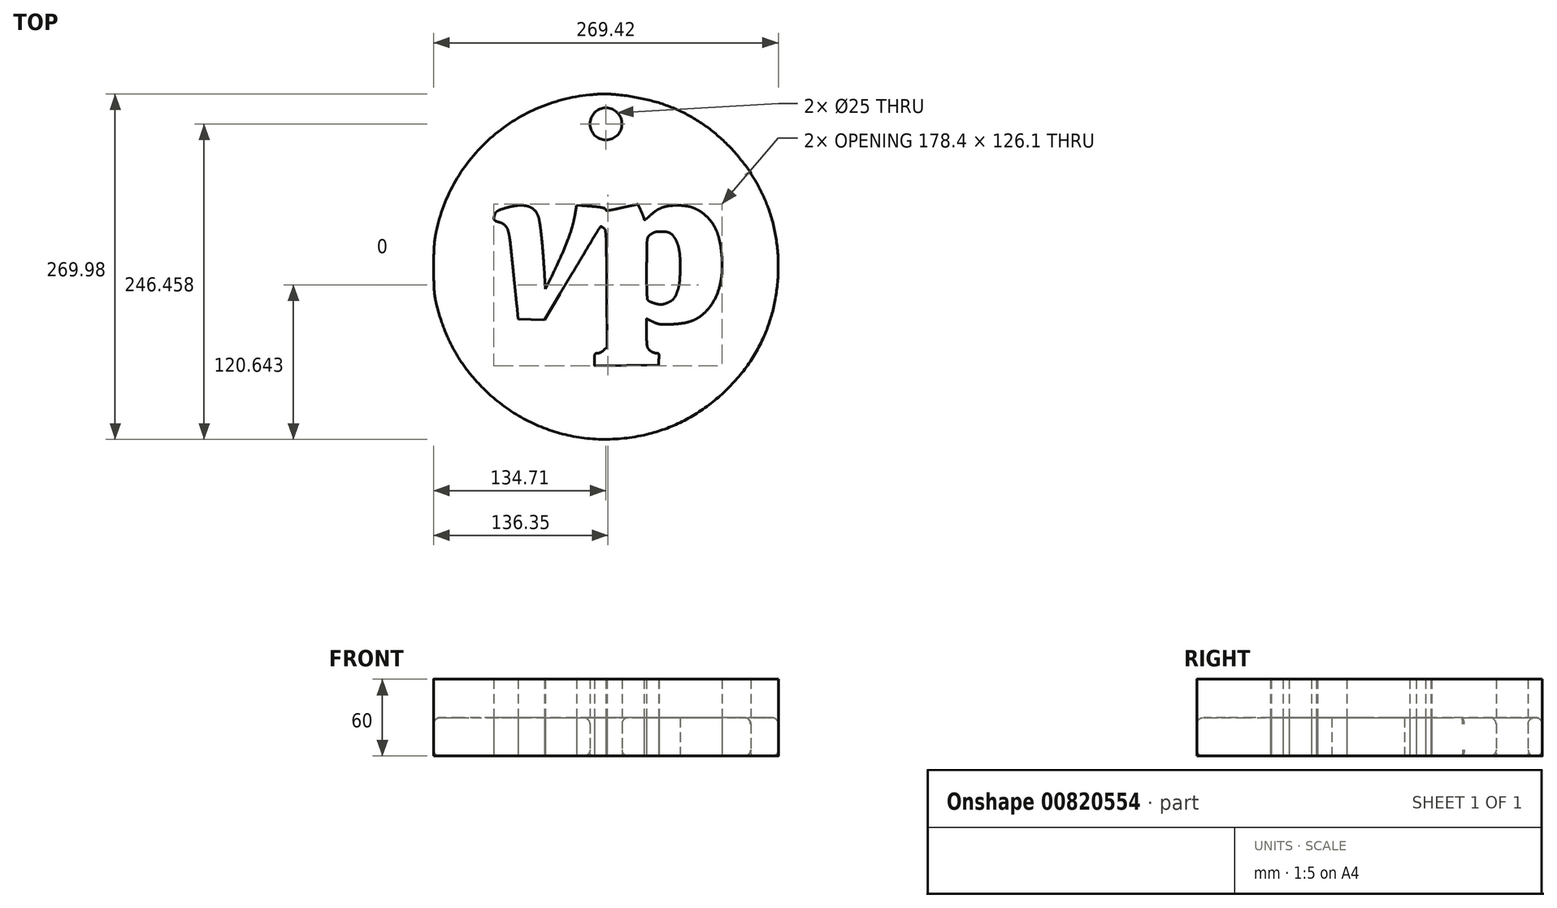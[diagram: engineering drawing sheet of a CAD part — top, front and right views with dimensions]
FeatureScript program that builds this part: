
annotation { "Feature Type Name" : "Feature", "Feature Type Description" : "" }
export const myFeature = defineFeature(function(context is Context, id is Id, definition is map)
    precondition{}
    {
        {
            var Q0;
            Q0=qCreatedBy(makeId("Top.planeOp"),FACE);
            var sketch = newSketch(context, id + "F0", { "sketchPlane" : qUnion([Q0])});
            skArc(sketch, "E0", {"start": v(-12.8, 134.12) * mm, "mid": v(-33.97, 130.4) * mm, "end": v(-54.29, 123.36) * mm});
            skArc(sketch, "E1", {"start": v(-54.29, 123.36) * mm, "mid": v(-73.28, 113.18) * mm, "end": v(-90.43, 100.15) * mm});
            skArc(sketch, "E2", {"start": v(-90.43, 100.15) * mm, "mid": v(-105.3, 84.59) * mm, "end": v(-117.52, 66.88) * mm});
            skArc(sketch, "E3", {"start": v(-117.52, 66.88) * mm, "mid": v(-126.75, 47.53) * mm, "end": v(-132.77, 26.96) * mm});
            skArc(sketch, "E4", {"start": v(-132.77, 26.96) * mm, "mid": v(-133.74, 21.22) * mm, "end": v(-134.27, 15.41) * mm});
            skArc(sketch, "E5", {"start": v(-134.27, 15.41) * mm, "mid": v(-134.6, 7.1) * mm, "end": v(-134.7, -1.22) * mm});
            skArc(sketch, "E6", {"start": v(-134.7, -1.22) * mm, "mid": v(-134.6, -9.46) * mm, "end": v(-134.26, -17.69) * mm});
            skArc(sketch, "E7", {"start": v(-134.26, -17.69) * mm, "mid": v(-133.73, -23.05) * mm, "end": v(-132.73, -28.35) * mm});
            skArc(sketch, "E8", {"start": v(-132.73, -28.35) * mm, "mid": v(-130.15, -37.94) * mm, "end": v(-126.97, -47.34) * mm});
            skArc(sketch, "E9", {"start": v(-126.97, -47.34) * mm, "mid": v(-123.33, -56.1) * mm, "end": v(-119.06, -64.58) * mm});
            skArc(sketch, "E10", {"start": v(-119.06, -64.58) * mm, "mid": v(-114.25, -72.64) * mm, "end": v(-108.86, -80.33) * mm});
            skArc(sketch, "E11", {"start": v(-108.86, -80.33) * mm, "mid": v(-102.8, -87.8) * mm, "end": v(-96.25, -94.83) * mm});
            skArc(sketch, "E12", {"start": v(-96.25, -94.83) * mm, "mid": v(-82.95, -106.58) * mm, "end": v(-68.27, -116.56) * mm});
            skArc(sketch, "E13", {"start": v(-68.27, -116.56) * mm, "mid": v(-52.65, -124.44) * mm, "end": v(-36.12, -130.2) * mm});
            skArc(sketch, "E14", {"start": v(-36.12, -130.2) * mm, "mid": v(-18.96, -133.74) * mm, "end": v(-1.48, -134.98) * mm});
            skArc(sketch, "E15", {"start": v(-1.48, -134.98) * mm, "mid": v(16.29, -133.96) * mm, "end": v(33.8, -130.7) * mm});
            skArc(sketch, "E16", {"start": v(33.8, -130.7) * mm, "mid": v(47.8, -126.28) * mm, "end": v(61.2, -120.25) * mm});
            skArc(sketch, "E17", {"start": v(61.2, -120.25) * mm, "mid": v(74.24, -112.5) * mm, "end": v(86.38, -103.4) * mm});
            skArc(sketch, "E18", {"start": v(86.38, -103.4) * mm, "mid": v(97.5, -93.04) * mm, "end": v(107.44, -81.55) * mm});
            skArc(sketch, "E19", {"start": v(107.44, -81.55) * mm, "mid": v(115.81, -69.37) * mm, "end": v(122.71, -56.3) * mm});
            skArc(sketch, "E20", {"start": v(122.71, -56.3) * mm, "mid": v(127.5, -44.26) * mm, "end": v(131.05, -31.81) * mm});
            skArc(sketch, "E21", {"start": v(131.05, -31.81) * mm, "mid": v(133.43, -18.82) * mm, "end": v(134.6, -5.67) * mm});
            skArc(sketch, "E22", {"start": v(134.6, -5.67) * mm, "mid": v(134.51, 7.53) * mm, "end": v(133.2, 20.65) * mm});
            skArc(sketch, "E23", {"start": v(133.2, 20.65) * mm, "mid": v(130.67, 33.3) * mm, "end": v(126.9, 45.64) * mm});
            skArc(sketch, "E24", {"start": v(126.9, 45.64) * mm, "mid": v(125.79, 48.55) * mm, "end": v(124.59, 51.42) * mm});
            skArc(sketch, "E25", {"start": v(124.59, 51.42) * mm, "mid": v(123.09, 54.78) * mm, "end": v(121.52, 58.1) * mm});
            skArc(sketch, "E26", {"start": v(121.52, 58.1) * mm, "mid": v(119.97, 61.25) * mm, "end": v(118.36, 64.35) * mm});
            skArc(sketch, "E27", {"start": v(118.36, 64.35) * mm, "mid": v(117.17, 66.46) * mm, "end": v(115.86, 68.5) * mm});
            skArc(sketch, "E28", {"start": v(115.86, 68.5) * mm, "mid": v(115.38, 69.22) * mm, "end": v(114.9, 69.95) * mm});
            skArc(sketch, "E29", {"start": v(114.9, 69.95) * mm, "mid": v(114.5, 70.6) * mm, "end": v(114.1, 71.25) * mm});
            skArc(sketch, "E30", {"start": v(114.1, 71.25) * mm, "mid": v(113.78, 71.8) * mm, "end": v(113.46, 72.36) * mm});
            skArc(sketch, "E31", {"start": v(113.46, 72.36) * mm, "mid": v(113.4, 72.52) * mm, "end": v(113.37, 72.7) * mm});
            skArc(sketch, "E32", {"start": v(113.37, 72.7) * mm, "mid": v(113.25, 73.44) * mm, "end": v(112.89, 74.1) * mm});
            skArc(sketch, "E33", {"start": v(112.89, 74.1) * mm, "mid": v(110.07, 77.7) * mm, "end": v(107.23, 81.3) * mm});
            skArc(sketch, "E34", {"start": v(107.23, 81.3) * mm, "mid": v(104.44, 84.76) * mm, "end": v(101.6, 88.17) * mm});
            skArc(sketch, "E35", {"start": v(101.6, 88.17) * mm, "mid": v(99.42, 90.68) * mm, "end": v(97.16, 93.11) * mm});
            skArc(sketch, "E36", {"start": v(97.16, 93.11) * mm, "mid": v(88.23, 101.61) * mm, "end": v(78.6, 109.3) * mm});
            skArc(sketch, "E37", {"start": v(78.6, 109.3) * mm, "mid": v(68.62, 115.87) * mm, "end": v(58.07, 121.46) * mm});
            skArc(sketch, "E38", {"start": v(58.07, 121.46) * mm, "mid": v(46.83, 126.1) * mm, "end": v(35.2, 129.69) * mm});
            skArc(sketch, "E39", {"start": v(35.2, 129.69) * mm, "mid": v(22.52, 132.43) * mm, "end": v(9.67, 134.2) * mm});
            skArc(sketch, "E40", {"start": v(9.67, 134.2) * mm, "mid": v(6.1, 134.53) * mm, "end": v(2.54, 134.84) * mm});
            skArc(sketch, "E41", {"start": v(2.54, 134.84) * mm, "mid": v(0.68, 134.95) * mm, "end": v(-1.18, 134.99) * mm});
            skArc(sketch, "E42", {"start": v(-1.18, 134.99) * mm, "mid": v(-3.09, 134.94) * mm, "end": v(-5, 134.82) * mm});
            skArc(sketch, "E43", {"start": v(-5, 134.82) * mm, "mid": v(-8.9, 134.48) * mm, "end": v(-12.8, 134.12) * mm});
            skArc(sketch, "E44", {"start": v(27.46, 43.43) * mm, "mid": v(27.93, 42.36) * mm, "end": v(28.4, 41.28) * mm});
            skArc(sketch, "E45", {"start": v(28.4, 41.28) * mm, "mid": v(28.8, 40.26) * mm, "end": v(29.19, 39.24) * mm});
            skArc(sketch, "E46", {"start": v(29.19, 39.24) * mm, "mid": v(29.5, 38.38) * mm, "end": v(29.78, 37.52) * mm});
            skArc(sketch, "E47", {"start": v(29.78, 37.52) * mm, "mid": v(29.88, 37.11) * mm, "end": v(29.9, 36.7) * mm});
            skArc(sketch, "E48", {"start": v(29.9, 36.7) * mm, "mid": v(30.02, 36.5) * mm, "end": v(30.24, 36.5) * mm});
            skArc(sketch, "E49", {"start": v(30.24, 36.5) * mm, "mid": v(30.8, 36.78) * mm, "end": v(31.32, 37.12) * mm});
            skArc(sketch, "E50", {"start": v(31.32, 37.12) * mm, "mid": v(32.11, 37.7) * mm, "end": v(32.87, 38.32) * mm});
            skArc(sketch, "E51", {"start": v(32.87, 38.32) * mm, "mid": v(33.8, 39.16) * mm, "end": v(34.72, 40.02) * mm});
            skArc(sketch, "E52", {"start": v(34.72, 40.02) * mm, "mid": v(36.88, 41.95) * mm, "end": v(39.2, 43.67) * mm});
            skArc(sketch, "E53", {"start": v(39.2, 43.67) * mm, "mid": v(41.45, 45) * mm, "end": v(43.85, 46.07) * mm});
            skArc(sketch, "E54", {"start": v(43.85, 46.07) * mm, "mid": v(46.47, 46.88) * mm, "end": v(49.17, 47.4) * mm});
            skArc(sketch, "E55", {"start": v(49.17, 47.4) * mm, "mid": v(52.42, 47.72) * mm, "end": v(55.69, 47.83) * mm});
            skArc(sketch, "E56", {"start": v(55.69, 47.83) * mm, "mid": v(59.02, 47.72) * mm, "end": v(62.34, 47.38) * mm});
            skArc(sketch, "E57", {"start": v(62.34, 47.38) * mm, "mid": v(65.17, 46.85) * mm, "end": v(67.93, 46.03) * mm});
            skArc(sketch, "E58", {"start": v(67.93, 46.03) * mm, "mid": v(70.5, 44.95) * mm, "end": v(72.93, 43.6) * mm});
            skArc(sketch, "E59", {"start": v(72.93, 43.6) * mm, "mid": v(75.43, 41.9) * mm, "end": v(77.77, 39.97) * mm});
            skArc(sketch, "E60", {"start": v(77.77, 39.97) * mm, "mid": v(80.12, 37.67) * mm, "end": v(82.25, 35.16) * mm});
            skArc(sketch, "E61", {"start": v(82.25, 35.16) * mm, "mid": v(84.07, 32.52) * mm, "end": v(85.6, 29.71) * mm});
            skArc(sketch, "E62", {"start": v(85.6, 29.71) * mm, "mid": v(86.97, 26.54) * mm, "end": v(88.03, 23.24) * mm});
            skArc(sketch, "E63", {"start": v(88.03, 23.24) * mm, "mid": v(88.99, 19.3) * mm, "end": v(89.7, 15.32) * mm});
            skArc(sketch, "E64", {"start": v(89.7, 15.32) * mm, "mid": v(90.58, 7.55) * mm, "end": v(90.84, -0.27) * mm});
            skArc(sketch, "E65", {"start": v(90.84, -0.27) * mm, "mid": v(90.4, -7.21) * mm, "end": v(89.21, -14.07) * mm});
            skArc(sketch, "E66", {"start": v(89.21, -14.07) * mm, "mid": v(87.42, -20.08) * mm, "end": v(84.88, -25.8) * mm});
            skArc(sketch, "E67", {"start": v(84.88, -25.8) * mm, "mid": v(81.8, -30.79) * mm, "end": v(77.98, -35.24) * mm});
            skArc(sketch, "E68", {"start": v(77.98, -35.24) * mm, "mid": v(75.47, -37.52) * mm, "end": v(72.75, -39.55) * mm});
            skArc(sketch, "E69", {"start": v(72.75, -39.55) * mm, "mid": v(70.03, -41.17) * mm, "end": v(67.14, -42.45) * mm});
            skArc(sketch, "E70", {"start": v(67.14, -42.45) * mm, "mid": v(63.81, -43.5) * mm, "end": v(60.4, -44.21) * mm});
            skArc(sketch, "E71", {"start": v(60.4, -44.21) * mm, "mid": v(56.05, -44.77) * mm, "end": v(51.67, -45.1) * mm});
            skArc(sketch, "E72", {"start": v(51.67, -45.1) * mm, "mid": v(48.8, -45.22) * mm, "end": v(45.94, -45.3) * mm});
            skArc(sketch, "E73", {"start": v(45.94, -45.3) * mm, "mid": v(44.32, -45.27) * mm, "end": v(42.7, -45.13) * mm});
            skArc(sketch, "E74", {"start": v(42.7, -45.13) * mm, "mid": v(41.4, -44.9) * mm, "end": v(40.13, -44.54) * mm});
            skArc(sketch, "E75", {"start": v(40.13, -44.54) * mm, "mid": v(38.6, -43.98) * mm, "end": v(37.11, -43.32) * mm});
            skArc(sketch, "E76", {"start": v(37.11, -43.32) * mm, "mid": v(36.18, -42.88) * mm, "end": v(35.25, -42.44) * mm});
            skArc(sketch, "E77", {"start": v(35.25, -42.44) * mm, "mid": v(34.42, -42.04) * mm, "end": v(33.6, -41.65) * mm});
            skArc(sketch, "E78", {"start": v(33.6, -41.65) * mm, "mid": v(32.9, -41.3) * mm, "end": v(32.2, -40.97) * mm});
            skArc(sketch, "E79", {"start": v(32.2, -40.97) * mm, "mid": v(32.02, -40.88) * mm, "end": v(31.85, -40.78) * mm});
            skArc(sketch, "E80", {"start": v(31.85, -40.78) * mm, "mid": v(31.73, -40.77) * mm, "end": v(31.66, -40.88) * mm});
            skArc(sketch, "E81", {"start": v(31.66, -40.88) * mm, "mid": v(31.62, -42.43) * mm, "end": v(31.6, -43.98) * mm});
            skArc(sketch, "E82", {"start": v(31.6, -43.98) * mm, "mid": v(31.58, -45.82) * mm, "end": v(31.58, -47.67) * mm});
            skArc(sketch, "E83", {"start": v(31.58, -47.67) * mm, "mid": v(31.62, -49.89) * mm, "end": v(31.66, -52.1) * mm});
            skArc(sketch, "E84", {"start": v(31.66, -52.1) * mm, "mid": v(31.77, -55.76) * mm, "end": v(31.9, -59.42) * mm});
            skArc(sketch, "E85", {"start": v(31.9, -59.42) * mm, "mid": v(32.03, -60.9) * mm, "end": v(32.27, -62.38) * mm});
            skArc(sketch, "E86", {"start": v(32.27, -62.38) * mm, "mid": v(32.56, -63.3) * mm, "end": v(33.02, -64.15) * mm});
            skArc(sketch, "E87", {"start": v(33.02, -64.15) * mm, "mid": v(33.69, -64.98) * mm, "end": v(34.46, -65.7) * mm});
            skArc(sketch, "E88", {"start": v(34.46, -65.7) * mm, "mid": v(35.01, -66.1) * mm, "end": v(35.6, -66.45) * mm});
            skArc(sketch, "E89", {"start": v(35.6, -66.45) * mm, "mid": v(36.25, -66.78) * mm, "end": v(36.92, -67.08) * mm});
            skArc(sketch, "E90", {"start": v(36.92, -67.08) * mm, "mid": v(37.57, -67.32) * mm, "end": v(38.23, -67.52) * mm});
            skArc(sketch, "E91", {"start": v(38.23, -67.52) * mm, "mid": v(38.77, -67.62) * mm, "end": v(39.31, -67.66) * mm});
            skArc(sketch, "E92", {"start": v(39.31, -67.66) * mm, "mid": v(39.98, -67.7) * mm, "end": v(40.64, -67.82) * mm});
            skArc(sketch, "E93", {"start": v(40.64, -67.82) * mm, "mid": v(41.02, -68.01) * mm, "end": v(41.27, -68.35) * mm});
            skArc(sketch, "E94", {"start": v(41.27, -68.35) * mm, "mid": v(41.44, -68.89) * mm, "end": v(41.49, -69.45) * mm});
            skArc(sketch, "E95", {"start": v(41.49, -69.45) * mm, "mid": v(41.44, -70.86) * mm, "end": v(41.37, -72.27) * mm});
            skLineSegment(sketch, "E96", {"start": v(41.37, -72.27) * mm, "end": v(41.07, -76.88) * mm});
            skLineSegment(sketch, "E97", {"start": v(41.07, -76.88) * mm, "end": v(16.08, -77.14) * mm});
            skLineSegment(sketch, "E98", {"start": v(16.08, -77.14) * mm, "end": v(-8.9, -77.4) * mm});
            skLineSegment(sketch, "E99", {"start": v(-8.9, -77.4) * mm, "end": v(-8.9, -72.53) * mm});
            skArc(sketch, "E100", {"start": v(-8.9, -72.53) * mm, "mid": v(-8.9, -71.04) * mm, "end": v(-8.85, -69.55) * mm});
            skArc(sketch, "E101", {"start": v(-8.85, -69.55) * mm, "mid": v(-8.76, -68.95) * mm, "end": v(-8.54, -68.38) * mm});
            skArc(sketch, "E102", {"start": v(-8.54, -68.38) * mm, "mid": v(-8.26, -68.03) * mm, "end": v(-7.85, -67.83) * mm});
            skArc(sketch, "E103", {"start": v(-7.85, -67.83) * mm, "mid": v(-7.15, -67.7) * mm, "end": v(-6.44, -67.66) * mm});
            skArc(sketch, "E104", {"start": v(-6.44, -67.66) * mm, "mid": v(-5.87, -67.62) * mm, "end": v(-5.32, -67.49) * mm});
            skArc(sketch, "E105", {"start": v(-5.32, -67.49) * mm, "mid": v(-4.64, -67.24) * mm, "end": v(-3.99, -66.95) * mm});
            skArc(sketch, "E106", {"start": v(-3.99, -66.95) * mm, "mid": v(-3.31, -66.59) * mm, "end": v(-2.66, -66.17) * mm});
            skArc(sketch, "E107", {"start": v(-2.66, -66.17) * mm, "mid": v(-2.1, -65.74) * mm, "end": v(-1.56, -65.25) * mm});
            skLineSegment(sketch, "E108", {"start": v(-1.56, -65.25) * mm, "end": v(0.85, -62.84) * mm});
            skLineSegment(sketch, "E109", {"start": v(0.85, -62.84) * mm, "end": v(0.58, -17.13) * mm});
            skArc(sketch, "E110", {"start": v(0.58, -17.13) * mm, "mid": v(0.48, -2.6) * mm, "end": v(0.37, 11.92) * mm});
            skArc(sketch, "E111", {"start": v(0.37, 11.92) * mm, "mid": v(0.28, 17.16) * mm, "end": v(0.08, 22.4) * mm});
            skArc(sketch, "E112", {"start": v(0.08, 22.4) * mm, "mid": v(-0.1, 25.2) * mm, "end": v(-0.4, 27.97) * mm});
            skArc(sketch, "E113", {"start": v(-0.4, 27.97) * mm, "mid": v(-0.78, 29.08) * mm, "end": v(-1.57, 29.95) * mm});
            skArc(sketch, "E114", {"start": v(-1.57, 29.95) * mm, "mid": v(-1.95, 30.22) * mm, "end": v(-2.34, 30.48) * mm});
            skArc(sketch, "E115", {"start": v(-2.34, 30.48) * mm, "mid": v(-2.7, 30.7) * mm, "end": v(-3.07, 30.93) * mm});
            skArc(sketch, "E116", {"start": v(-3.07, 30.93) * mm, "mid": v(-3.38, 31.1) * mm, "end": v(-3.7, 31.26) * mm});
            skArc(sketch, "E117", {"start": v(-3.7, 31.26) * mm, "mid": v(-3.85, 31.31) * mm, "end": v(-4.02, 31.33) * mm});
            skArc(sketch, "E118", {"start": v(-4.02, 31.33) * mm, "mid": v(-4.2, 31.28) * mm, "end": v(-4.35, 31.15) * mm});
            skArc(sketch, "E119", {"start": v(-4.35, 31.15) * mm, "mid": v(-5.45, 29.44) * mm, "end": v(-6.55, 27.73) * mm});
            skArc(sketch, "E120", {"start": v(-6.55, 27.73) * mm, "mid": v(-7.79, 25.76) * mm, "end": v(-9.01, 23.77) * mm});
            skArc(sketch, "E121", {"start": v(-9.01, 23.77) * mm, "mid": v(-10.43, 21.43) * mm, "end": v(-11.84, 19.07) * mm});
            skArc(sketch, "E122", {"start": v(-11.84, 19.07) * mm, "mid": v(-14.73, 14.19) * mm, "end": v(-17.63, 9.3) * mm});
            skArc(sketch, "E123", {"start": v(-17.63, 9.3) * mm, "mid": v(-19.57, 6.04) * mm, "end": v(-21.52, 2.78) * mm});
            skArc(sketch, "E124", {"start": v(-21.52, 2.78) * mm, "mid": v(-23.82, -1.06) * mm, "end": v(-26.12, -4.9) * mm});
            skArc(sketch, "E125", {"start": v(-26.12, -4.9) * mm, "mid": v(-31.08, -13.15) * mm, "end": v(-36.04, -21.4) * mm});
            skLineSegment(sketch, "E126", {"start": v(-36.04, -21.4) * mm, "end": v(-48.14, -41.52) * mm});
            skLineSegment(sketch, "E127", {"start": v(-48.14, -41.52) * mm, "end": v(-58.37, -41.24) * mm});
            skLineSegment(sketch, "E128", {"start": v(-58.37, -41.24) * mm, "end": v(-68.6, -40.97) * mm});
            skLineSegment(sketch, "E129", {"start": v(-68.6, -40.97) * mm, "end": v(-69.72, -30.3) * mm});
            skArc(sketch, "E130", {"start": v(-69.72, -30.3) * mm, "mid": v(-69.99, -27.7) * mm, "end": v(-70.25, -25.12) * mm});
            skArc(sketch, "E131", {"start": v(-70.25, -25.12) * mm, "mid": v(-70.6, -21.66) * mm, "end": v(-70.96, -18.21) * mm});
            skArc(sketch, "E132", {"start": v(-70.96, -18.21) * mm, "mid": v(-71.34, -14.53) * mm, "end": v(-71.71, -10.85) * mm});
            skArc(sketch, "E133", {"start": v(-71.71, -10.85) * mm, "mid": v(-72.05, -7.5) * mm, "end": v(-72.39, -4.14) * mm});
            skArc(sketch, "E134", {"start": v(-72.39, -4.14) * mm, "mid": v(-73.64, 8.02) * mm, "end": v(-74.96, 20.19) * mm});
            skArc(sketch, "E135", {"start": v(-74.96, 20.19) * mm, "mid": v(-75.6, 24.34) * mm, "end": v(-76.58, 28.42) * mm});
            skArc(sketch, "E136", {"start": v(-76.58, 28.42) * mm, "mid": v(-77.55, 30.6) * mm, "end": v(-79.1, 32.42) * mm});
            skArc(sketch, "E137", {"start": v(-79.1, 32.42) * mm, "mid": v(-81.14, 33.82) * mm, "end": v(-83.48, 34.67) * mm});
            skArc(sketch, "E138", {"start": v(-83.48, 34.67) * mm, "mid": v(-84.8, 35.04) * mm, "end": v(-86.1, 35.52) * mm});
            skArc(sketch, "E139", {"start": v(-86.1, 35.52) * mm, "mid": v(-86.8, 35.99) * mm, "end": v(-87.3, 36.67) * mm});
            skArc(sketch, "E140", {"start": v(-87.3, 36.67) * mm, "mid": v(-87.54, 37.52) * mm, "end": v(-87.5, 38.4) * mm});
            skArc(sketch, "E141", {"start": v(-87.5, 38.4) * mm, "mid": v(-87.12, 39.86) * mm, "end": v(-86.64, 41.3) * mm});
            skArc(sketch, "E142", {"start": v(-86.64, 41.3) * mm, "mid": v(-86.3, 41.96) * mm, "end": v(-85.83, 42.54) * mm});
            skArc(sketch, "E143", {"start": v(-85.83, 42.54) * mm, "mid": v(-85.19, 43.1) * mm, "end": v(-84.47, 43.57) * mm});
            skArc(sketch, "E144", {"start": v(-84.47, 43.57) * mm, "mid": v(-83.4, 44.1) * mm, "end": v(-82.27, 44.55) * mm});
            skArc(sketch, "E145", {"start": v(-82.27, 44.55) * mm, "mid": v(-80.46, 45.16) * mm, "end": v(-78.63, 45.72) * mm});
            skArc(sketch, "E146", {"start": v(-78.63, 45.72) * mm, "mid": v(-74.03, 46.89) * mm, "end": v(-69.34, 47.68) * mm});
            skArc(sketch, "E147", {"start": v(-69.34, 47.68) * mm, "mid": v(-65.65, 47.83) * mm, "end": v(-61.99, 47.36) * mm});
            skArc(sketch, "E148", {"start": v(-61.99, 47.36) * mm, "mid": v(-59.17, 46.41) * mm, "end": v(-56.65, 44.84) * mm});
            skArc(sketch, "E149", {"start": v(-56.65, 44.84) * mm, "mid": v(-54.67, 42.78) * mm, "end": v(-53.28, 40.29) * mm});
            skArc(sketch, "E150", {"start": v(-53.28, 40.29) * mm, "mid": v(-52.5, 37.98) * mm, "end": v(-52, 35.6) * mm});
            skArc(sketch, "E151", {"start": v(-52, 35.6) * mm, "mid": v(-51.32, 31.17) * mm, "end": v(-50.74, 26.71) * mm});
            skArc(sketch, "E152", {"start": v(-50.74, 26.71) * mm, "mid": v(-50.08, 20.76) * mm, "end": v(-49.53, 14.8) * mm});
            skArc(sketch, "E153", {"start": v(-49.53, 14.8) * mm, "mid": v(-48.92, 7.05) * mm, "end": v(-48.37, -0.7) * mm});
            skLineSegment(sketch, "E154", {"start": v(-48.37, -0.7) * mm, "end": v(-47.23, -17.68) * mm});
            skLineSegment(sketch, "E155", {"start": v(-47.23, -17.68) * mm, "end": v(-43.5, -9.92) * mm});
            skArc(sketch, "E156", {"start": v(-43.5, -9.92) * mm, "mid": v(-39.32, -1.12) * mm, "end": v(-35.25, 7.73) * mm});
            skArc(sketch, "E157", {"start": v(-35.25, 7.73) * mm, "mid": v(-32.43, 14.2) * mm, "end": v(-29.82, 20.76) * mm});
            skArc(sketch, "E158", {"start": v(-29.82, 20.76) * mm, "mid": v(-27.96, 25.96) * mm, "end": v(-26.31, 31.24) * mm});
            skArc(sketch, "E159", {"start": v(-26.31, 31.24) * mm, "mid": v(-25.13, 35.87) * mm, "end": v(-24.25, 40.57) * mm});
            skLineSegment(sketch, "E160", {"start": v(-24.25, 40.57) * mm, "end": v(-23.09, 48.03) * mm});
            skLineSegment(sketch, "E161", {"start": v(-23.09, 48.03) * mm, "end": v(-14.79, 47.39) * mm});
            skArc(sketch, "E162", {"start": v(-14.79, 47.39) * mm, "mid": v(-11.04, 47.08) * mm, "end": v(-7.3, 46.73) * mm});
            skArc(sketch, "E163", {"start": v(-7.3, 46.73) * mm, "mid": v(-5.22, 46.48) * mm, "end": v(-3.16, 46.12) * mm});
            skArc(sketch, "E164", {"start": v(-3.16, 46.12) * mm, "mid": v(-1.98, 45.82) * mm, "end": v(-0.83, 45.4) * mm});
            skArc(sketch, "E165", {"start": v(-0.83, 45.4) * mm, "mid": v(-0.35, 45.01) * mm, "end": v(-0.18, 44.42) * mm});
            skArc(sketch, "E166", {"start": v(-0.18, 44.42) * mm, "mid": v(-0.05, 44.08) * mm, "end": v(0.25, 43.9) * mm});
            skArc(sketch, "E167", {"start": v(0.25, 43.9) * mm, "mid": v(0.92, 43.82) * mm, "end": v(1.6, 43.83) * mm});
            skArc(sketch, "E168", {"start": v(1.6, 43.83) * mm, "mid": v(2.8, 43.95) * mm, "end": v(4, 44.16) * mm});
            skArc(sketch, "E169", {"start": v(4, 44.16) * mm, "mid": v(6.16, 44.6) * mm, "end": v(8.32, 45.07) * mm});
            skArc(sketch, "E170", {"start": v(8.32, 45.07) * mm, "mid": v(10.08, 45.46) * mm, "end": v(11.85, 45.85) * mm});
            skArc(sketch, "E171", {"start": v(11.85, 45.85) * mm, "mid": v(13.65, 46.25) * mm, "end": v(15.45, 46.64) * mm});
            skArc(sketch, "E172", {"start": v(15.45, 46.64) * mm, "mid": v(17.05, 47) * mm, "end": v(18.64, 47.34) * mm});
            skArc(sketch, "E173", {"start": v(18.64, 47.34) * mm, "mid": v(19.67, 47.56) * mm, "end": v(20.7, 47.77) * mm});
            skArc(sketch, "E174", {"start": v(20.7, 47.77) * mm, "mid": v(21.44, 47.93) * mm, "end": v(22.2, 48.1) * mm});
            skArc(sketch, "E175", {"start": v(22.2, 48.1) * mm, "mid": v(22.84, 48.24) * mm, "end": v(23.5, 48.38) * mm});
            skArc(sketch, "E176", {"start": v(23.5, 48.38) * mm, "mid": v(24.06, 48.5) * mm, "end": v(24.62, 48.63) * mm});
            skArc(sketch, "E177", {"start": v(24.62, 48.63) * mm, "mid": v(24.7, 48.66) * mm, "end": v(24.79, 48.7) * mm});
            skArc(sketch, "E178", {"start": v(24.79, 48.7) * mm, "mid": v(24.86, 48.7) * mm, "end": v(24.91, 48.65) * mm});
            skArc(sketch, "E179", {"start": v(24.91, 48.65) * mm, "mid": v(25.29, 47.92) * mm, "end": v(25.66, 47.2) * mm});
            skArc(sketch, "E180", {"start": v(25.66, 47.2) * mm, "mid": v(26.08, 46.34) * mm, "end": v(26.5, 45.48) * mm});
            skArc(sketch, "E181", {"start": v(26.5, 45.48) * mm, "mid": v(26.98, 44.46) * mm, "end": v(27.46, 43.43) * mm});
            skArc(sketch, "E182", {"start": v(37.64, 26.65) * mm, "mid": v(37.28, 26.48) * mm, "end": v(36.92, 26.3) * mm});
            skArc(sketch, "E183", {"start": v(36.92, 26.3) * mm, "mid": v(36.44, 26.02) * mm, "end": v(35.97, 25.74) * mm});
            skArc(sketch, "E184", {"start": v(35.97, 25.74) * mm, "mid": v(35.46, 25.42) * mm, "end": v(34.95, 25.1) * mm});
            skArc(sketch, "E185", {"start": v(34.95, 25.1) * mm, "mid": v(34.49, 24.79) * mm, "end": v(34.03, 24.47) * mm});
            skArc(sketch, "E186", {"start": v(34.03, 24.47) * mm, "mid": v(33.28, 23.72) * mm, "end": v(32.78, 22.79) * mm});
            skArc(sketch, "E187", {"start": v(32.78, 22.79) * mm, "mid": v(32.4, 21.39) * mm, "end": v(32.18, 19.95) * mm});
            skArc(sketch, "E188", {"start": v(32.18, 19.95) * mm, "mid": v(32, 17.22) * mm, "end": v(31.92, 14.48) * mm});
            skArc(sketch, "E189", {"start": v(31.92, 14.48) * mm, "mid": v(31.86, 6.66) * mm, "end": v(31.82, -1.15) * mm});
            skArc(sketch, "E190", {"start": v(31.82, -1.15) * mm, "mid": v(31.8, -7.27) * mm, "end": v(31.83, -13.38) * mm});
            skArc(sketch, "E191", {"start": v(31.83, -13.38) * mm, "mid": v(31.88, -16.93) * mm, "end": v(32, -20.49) * mm});
            skArc(sketch, "E192", {"start": v(32, -20.49) * mm, "mid": v(32.14, -22.8) * mm, "end": v(32.33, -25.1) * mm});
            skArc(sketch, "E193", {"start": v(32.33, -25.1) * mm, "mid": v(32.54, -25.86) * mm, "end": v(33, -26.5) * mm});
            skArc(sketch, "E194", {"start": v(33, -26.5) * mm, "mid": v(33.37, -26.82) * mm, "end": v(33.78, -27.07) * mm});
            skArc(sketch, "E195", {"start": v(33.78, -27.07) * mm, "mid": v(34.5, -27.42) * mm, "end": v(35.22, -27.75) * mm});
            skArc(sketch, "E196", {"start": v(35.22, -27.75) * mm, "mid": v(36.09, -28.1) * mm, "end": v(36.96, -28.41) * mm});
            skArc(sketch, "E197", {"start": v(36.96, -28.41) * mm, "mid": v(37.87, -28.7) * mm, "end": v(38.78, -28.96) * mm});
            skArc(sketch, "E198", {"start": v(38.78, -28.96) * mm, "mid": v(40.07, -29.27) * mm, "end": v(41.38, -29.53) * mm});
            skArc(sketch, "E199", {"start": v(41.38, -29.53) * mm, "mid": v(42.32, -29.64) * mm, "end": v(43.26, -29.64) * mm});
            skArc(sketch, "E200", {"start": v(43.26, -29.64) * mm, "mid": v(44.2, -29.54) * mm, "end": v(45.13, -29.33) * mm});
            skArc(sketch, "E201", {"start": v(45.13, -29.33) * mm, "mid": v(46.42, -28.93) * mm, "end": v(47.68, -28.48) * mm});
            skArc(sketch, "E202", {"start": v(47.68, -28.48) * mm, "mid": v(49.35, -27.74) * mm, "end": v(50.95, -26.85) * mm});
            skArc(sketch, "E203", {"start": v(50.95, -26.85) * mm, "mid": v(52.15, -25.94) * mm, "end": v(53.17, -24.84) * mm});
            skArc(sketch, "E204", {"start": v(53.17, -24.84) * mm, "mid": v(54.12, -23.43) * mm, "end": v(54.87, -21.9) * mm});
            skArc(sketch, "E205", {"start": v(54.87, -21.9) * mm, "mid": v(55.74, -19.56) * mm, "end": v(56.51, -17.19) * mm});
            skArc(sketch, "E206", {"start": v(56.51, -17.19) * mm, "mid": v(57.21, -14.27) * mm, "end": v(57.6, -11.29) * mm});
            skArc(sketch, "E207", {"start": v(57.6, -11.29) * mm, "mid": v(57.9, -6.74) * mm, "end": v(58.04, -2.18) * mm});
            skArc(sketch, "E208", {"start": v(58.04, -2.18) * mm, "mid": v(58.03, 2.49) * mm, "end": v(57.87, 7.15) * mm});
            skArc(sketch, "E209", {"start": v(57.87, 7.15) * mm, "mid": v(57.56, 10.62) * mm, "end": v(56.99, 14.06) * mm});
            skArc(sketch, "E210", {"start": v(56.99, 14.06) * mm, "mid": v(56.47, 16.17) * mm, "end": v(55.78, 18.24) * mm});
            skArc(sketch, "E211", {"start": v(55.78, 18.24) * mm, "mid": v(54.98, 20.12) * mm, "end": v(54.01, 21.91) * mm});
            skArc(sketch, "E212", {"start": v(54.01, 21.91) * mm, "mid": v(53.02, 23.39) * mm, "end": v(51.87, 24.75) * mm});
            skArc(sketch, "E213", {"start": v(51.87, 24.75) * mm, "mid": v(50.78, 25.7) * mm, "end": v(49.53, 26.42) * mm});
            skArc(sketch, "E214", {"start": v(49.53, 26.42) * mm, "mid": v(48.37, 26.85) * mm, "end": v(47.15, 27.1) * mm});
            skArc(sketch, "E215", {"start": v(47.15, 27.1) * mm, "mid": v(45.35, 27.27) * mm, "end": v(43.54, 27.35) * mm});
            skArc(sketch, "E216", {"start": v(43.54, 27.35) * mm, "mid": v(41.73, 27.34) * mm, "end": v(39.93, 27.24) * mm});
            skArc(sketch, "E217", {"start": v(39.93, 27.24) * mm, "mid": v(38.76, 27.04) * mm, "end": v(37.64, 26.65) * mm});
            skCircle(sketch, "E218", {"center": v(0, 111.47) * mm, "radius": 12.5 * mm});
            skSolve(sketch);
        }
        {
            var Q0;
            Q0=makeQuery(id+"F0.imprint","IMPRINT",FACE,{"disambiguationData":[TD([[makeQuery(id+"F0.imprint","IMPRINT",EDGE,{"derivedFrom":sQuery(id+"F0.wireOp",EDGE,"E0")}),1.0]])]});
            var Q1;
            Q1=makeQuery(id+"F0.imprint","IMPRINT",FACE,{"disambiguationData":[TD([[makeQuery(id+"F0.imprint","IMPRINT",EDGE,{"derivedFrom":sQuery(id+"F0.wireOp",EDGE,"E182")}),1.0]])]});
            extrude(context, id + "F1", {"entities" : qUnion([Q0, Q1]), "depth" : 30 * mm, "offsetDistance" : 25 * mm});
        }
        {
            var Q0;
            Q0=makeQuery(id+"F0.imprint","IMPRINT",FACE,{"disambiguationData":[TD([[makeQuery(id+"F0.imprint","IMPRINT",EDGE,{"derivedFrom":sQuery(id+"F0.wireOp",EDGE,"E44")}),-1.0]])]});
            extrude(context, id + "F2", {"entities" : qUnion([Q0]), "depth" : 60 * mm, "offsetDistance" : 25 * mm});
        }
        {
            var Q0;
            Q0=makeQuery(id+"F1.opExtrude","CAP_EDGE",EDGE,{"disambiguationData":[OSD([sQuery(id+"F0.wireOp",EDGE,"E218")])],"isStart":false});
            var Q1;
            Q1=makeQuery(id+"F1.opExtrude","CAP_EDGE",EDGE,{"disambiguationData":[OSD([sQuery(id+"F0.wireOp",EDGE,"E218")])],"isStart":true});
            var Q2;
            Q2=makeQuery(id+"F1.opExtrude","CAP_EDGE",EDGE,{"disambiguationData":[OSD([sQuery(id+"F0.wireOp",EDGE,"E11")])],"isStart":false});
            var Q3;
            Q3=makeQuery(id+"F1.opExtrude","CAP_EDGE",EDGE,{"disambiguationData":[OSD([sQuery(id+"F0.wireOp",EDGE,"E16")])],"isStart":true});
            fillet(context, id + "F3", {"entities" : qUnion([Q0, Q1, Q2, Q3]), "radius" : 5 * mm, "tangentPropagation" : true, "allowEdgeOverflow" : false});
        }
    });
